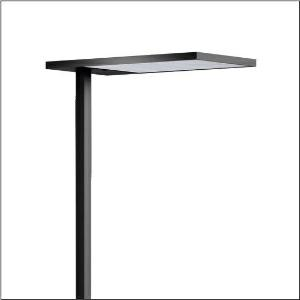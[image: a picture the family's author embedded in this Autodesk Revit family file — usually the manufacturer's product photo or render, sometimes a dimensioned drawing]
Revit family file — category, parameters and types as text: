
# Revit family: silica_r__21_floor_r_51mx53sg4db_4ec3
name_source: partatom
category: Lighting Fixtures
units: mm (PartAtom-declared; Revit-internal decimal feet)

## family parameters
Cut with Voids When Loaded = No
Host = Face
Light Source = No
Part Type = Normal
Room Calculation Point = No
Round Connector Dimension = Use Diameter
Shared = No

## types (1)
- Silica® 21 Floor R (1 x LED, 15000 lm, 106.4 W, 4000K)
    Apparent Load = 106 VA
    CIE Flux Codes = 54 86 97 13 100
    Color Rendering = 80
    Color Temperature = 4000K
    Default Elevation = 1800 mm
    Description = Silica® 21 Floor R, floorstanding luminaire, of PMMA, primary optical cover: prismatic diffuser, of PMMA, CAT 2 (L<= 3000cd/m²), light emission: indirect/direct distribution, primary light characteristic: symmetric, installation type: not mounted, LED, rated luminous flux: 15.000lm, luminous efficacy: 141lm/W, light colour: 840, colour temperature: 4000K, daylight-dependent control, mains connection: 230V, 50Hz, connection cable pre-assembled, cable length: 2,5m, rated input power: 106.4W, luminaire head, of aluminium, jet black (RAL 9005), length: 650mm, width: 350mm, supporting column, angular, of aluminium, jet black (RAL 9005), baseplate, of steel, jet black (RAL 9005), protection rating (complete): IP20, insulation class (complete): insulation class I (protective earthing), certification: CE, standard: EN 50419, packaging unit: 1 piece
    Height = 18 mm
    Lamp = 1 x LED
    Lamp Light Flux = 15000 lm
    Lamp Power = 106.4 W
    Lamp count = 1
    Length = 650 mm
    Luminous efficacy = 141 lm/W
    Manufacturer = Siteco
    ModVariant = No
    Model = 51MX53SG4DB
    Mounting Place = Floor
    Mounting Type = Freestanding
    Number of Poles = 1
    OnlyDefault = Yes
    Power Factor = 1
    Product Name = Silica® 21 Floor R
    Product group = floorstanding luminaire
    ProductGroupID = 1301
    Protection Class = Protection class I
    Protection Degree = IP 20
    RLX_Detail_Level = 1
    RLX_Emergency_Light_Flux = 0 lm
    RLX_Emergency_Type = 0
    RLX_Emergency_Type_DB = No
    RlxData = <blob elided: 21929 chars, md5=ddc6467e>
    Socket = socket
    Standby Power = 0 W
    System Light Flux = 15000 lm
    System Power = 106 W
    Type Comments = Product without accessories
    Type Image = l_1007011.jpg
    URL = http://relux.com
    VarID = ---
    Voltage = 0 V
    Weight = 0.00 kg
    Width = 350 mm

## geometry (parser evidence)
native form markers: Blend x4, Sweep x14
no freeform markers — native parametric forms only
